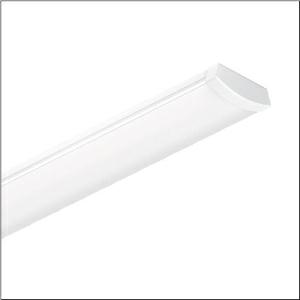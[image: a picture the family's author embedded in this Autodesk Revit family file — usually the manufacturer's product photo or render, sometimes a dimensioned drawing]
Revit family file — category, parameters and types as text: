
# Revit family: siluette_r__21_51ln12mnm70a3g_252a
name_source: partatom
category: Lighting Fixtures
units: mm (PartAtom-declared; Revit-internal decimal feet)

## family parameters
Cut with Voids When Loaded = No
Host = Face
Light Source = No
Part Type = Normal
Room Calculation Point = No
Round Connector Dimension = Use Diameter
Shared = No

## types (1)
- --- (1 x LED, 4320 lm, 28.8 W, 5000K)
    Apparent Load = 29 VA
    CIE Flux Codes = 43 73 92 94 100
    Color Rendering = 80
    Color Temperature = 5000K
    Default Elevation = 1800 mm
    Description = Siluette® 21, office luminaire, primary optical cover: enclosure, of PC, frosted, light emission: direct distribution, primary light characteristic: symmetric, installation type: suspended mounting, surface-mounted, LED, rated luminous flux: 7.000lm, luminous efficacy: 140lm/W, light colour: 830/840/850, colour temperature: 3000/4000/5000K, with terminal, 4-pole, mains connection: 220..240V, AC, 50/60Hz, rated input power: 50W, control gear: single battery element, housing, of sheet steel, white, length: 1.500mm, width: 152mm, height: 53mm, end cap, of PMMA, white, protection rating (complete): IP44, insulation class (complete): insulation class I (protective earthing), certification: CE, UKCA, protection symbol: D, permissible operating ambient temperature: -20..+40°C, standard: EN 60598-2-22, corresponds to IFS (International Featured Standards) requirements for safety and quality in the food industry, contact your sales advisor before using the luminaires in applications with unclear chemical exposure, large temperature fluctuations or condensation-forming humidity, packaging unit: 1 piece
    Height = 52 mm  [stored 0.170604 ft]
    Lamp = 1 x LED
    Lamp Light Flux = 4320 lm
    Lamp Power = 28.8 W
    Lamp count = 1
    Length = 1485 mm
    Luminous efficacy = 150 lm/W
    Manufacturer = Siteco
    ModVariant = No
    Model = 51LN12MNM70A3G
    Mounting Place = Ceiling
    Mounting Type = Pendant
    Number of Poles = 1
    OnlyDefault = Yes
    Power Factor = 1
    Product Name = Siluette® 21
    Product group = office luminaire | ceiling pendant
    ProductGroupID = 902
    Protection Class = Protection class I
    Protection Degree = IP 44
    RLX_Detail_Level = 1
    RLX_Emergency_Light_Flux = 0 lm
    RLX_Emergency_Type = 0
    RLX_Emergency_Type_DB = No
    RlxData = <blob elided: 20517 chars, md5=98da42fa>
    Socket = socket
    Standby Power = 0 W
    System Light Flux = 4320 lm
    System Power = 29 W
    Type Comments = individual setting: colour temperature 5000K, luminous flux: 61 % | (OFF | OFF | ON) | 200 mA
    Type Image = l_1296910.jpg
    URL = http://relux.com
    VarID = @adj_001783
    Voltage = 0 V
    Weight = 0.00 kg
    Width = 152 mm

note: [stored X ft] marks values corroborated as IEEE doubles in the binary element streams (Revit-internal decimal feet)

## geometry (parser evidence)
native form markers: Blend x4, Sweep x13
no freeform markers — native parametric forms only
